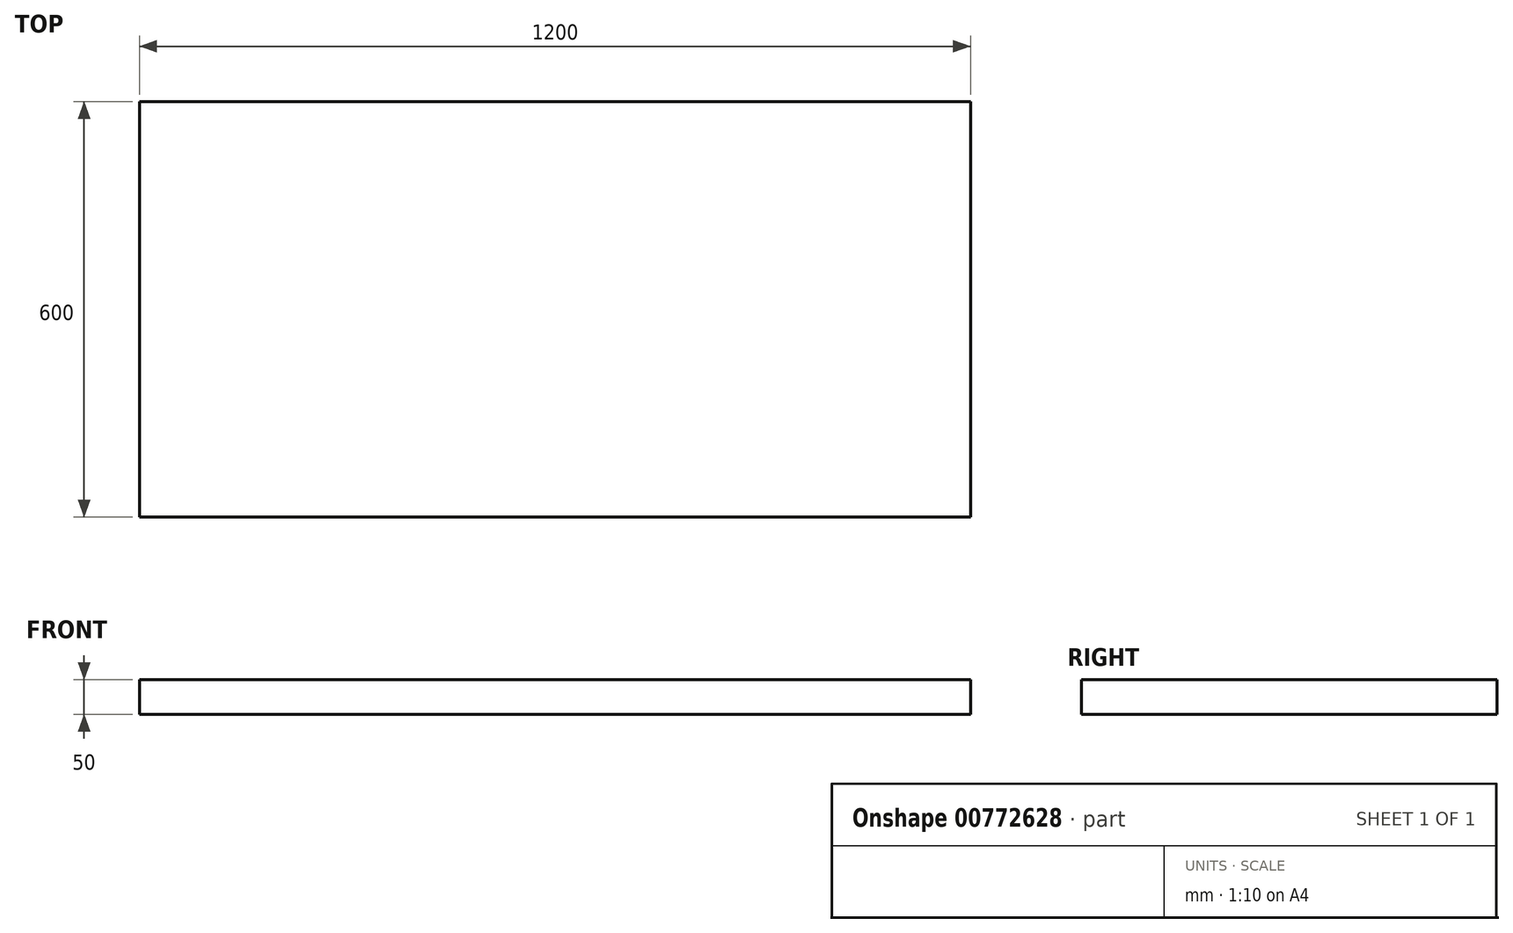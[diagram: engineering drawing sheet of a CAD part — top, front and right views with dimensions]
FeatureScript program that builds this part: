
annotation { "Feature Type Name" : "Feature", "Feature Type Description" : "" }
export const myFeature = defineFeature(function(context is Context, id is Id, definition is map)
    precondition{}
    {
        {
            var Q0;
            Q0=qCreatedBy(makeId("Top.planeOp"),FACE);
            var sketch = newSketch(context, id + "F0", { "sketchPlane" : qUnion([Q0])});
            skLineSegment(sketch, "E0.bottom", {"start": v(0, 0) * mm, "end": v(1200, 0) * mm});
            skLineSegment(sketch, "E0.top", {"start": v(0, 600) * mm, "end": v(1200, 600) * mm});
            skLineSegment(sketch, "E0.left", {"start": v(0, 0) * mm, "end": v(0, 600) * mm});
            skLineSegment(sketch, "E0.right", {"start": v(1200, 0) * mm, "end": v(1200, 600) * mm});
            skSolve(sketch);
        }
        {
            var Q0;
            Q0=makeQuery(id+"F0.imprint","IMPRINT",FACE,{"disambiguationData":[TD([[makeQuery(id+"F0.imprint","IMPRINT",EDGE,{"derivedFrom":sQuery(id+"F0.wireOp",EDGE,"E0.bottom")}),1.0]])]});
            extrude(context, id + "F1", {"entities" : qUnion([Q0]), "depth" : 50 * mm, "offsetDistance" : 25 * mm});
        }
    });
